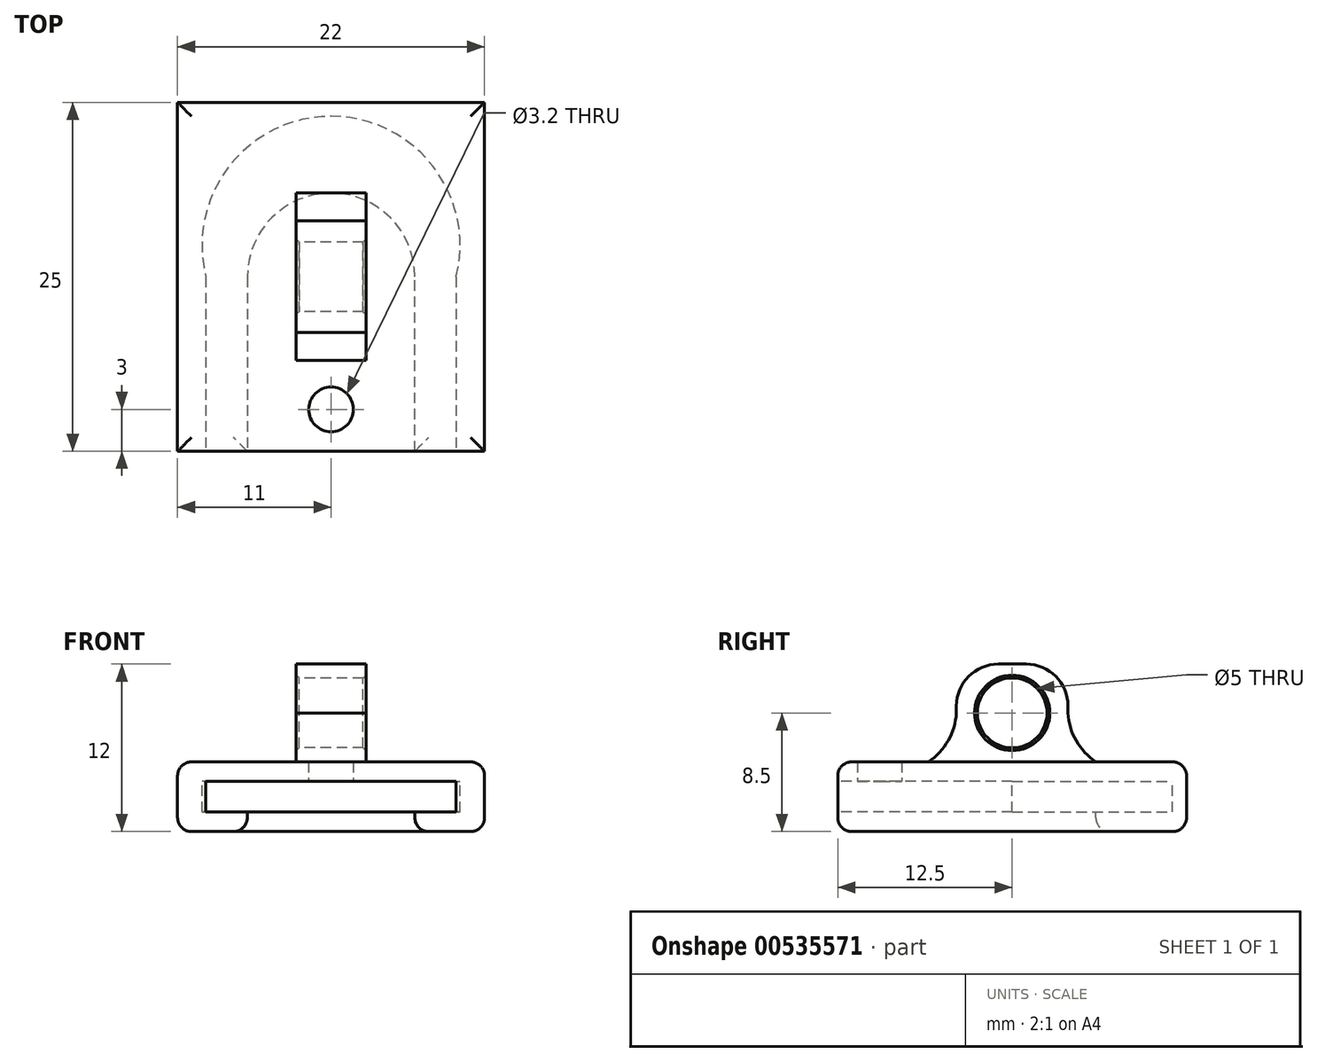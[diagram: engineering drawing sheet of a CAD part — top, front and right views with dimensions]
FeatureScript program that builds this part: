
annotation { "Feature Type Name" : "Feature", "Feature Type Description" : "" }
export const myFeature = defineFeature(function(context is Context, id is Id, definition is map)
    precondition{}
    {
        {
            var Q0;
            Q0=qCreatedBy(makeId("Top.planeOp"),FACE);
            var sketch = newSketch(context, id + "F0", { "sketchPlane" : qUnion([Q0])});
            skLineSegment(sketch, "E0.bottom", {"start": v(-11, 12.5) * mm, "end": v(11, 12.5) * mm});
            skLineSegment(sketch, "E0.top", {"start": v(-11, -12.5) * mm, "end": v(11, -12.5) * mm});
            skLineSegment(sketch, "E0.left", {"start": v(-11, 12.5) * mm, "end": v(-11, -12.5) * mm});
            skLineSegment(sketch, "E0.right", {"start": v(11, 12.5) * mm, "end": v(11, -12.5) * mm});
            skPoint(sketch, "E0.middle", {"position": v(0, 0) * mm});
            skSolve(sketch);
        }
        {
            var Q0;
            Q0 = qSketchRegion(id + "F0", true);
            extrude(context, id + "F1", {"entities" : qUnion([Q0]), "depth" : 5 * mm, "offsetDistance" : 25 * mm, "symmetric" : true});
        }
        {
            var Q0;
            Q0=qCreatedBy(makeId("Top.planeOp"),FACE);
            var sketch = newSketch(context, id + "F2", { "sketchPlane" : qUnion([Q0])});
            skCircle(sketch, "E1", {"center": v(0, 2.25) * mm, "radius": 9.25 * mm});
            skLineSegment(sketch, "E2", {"start": v(-8.97, 0) * mm, "end": v(-8.97, -12.5) * mm});
            skLineSegment(sketch, "E3", {"start": v(8.97, 0) * mm, "end": v(8.97, -12.5) * mm});
            skLineSegment(sketch, "E4", {"start": v(-8.97, -12.5) * mm, "end": v(8.97, -12.5) * mm});
            skSolve(sketch);
        }
        {
            var Q0;
            Q0 = qSketchRegion(id + "F2", true);
            extrude(context, id + "F3", {"entities" : qUnion([Q0]), "operationType" : NewBodyOperationType.REMOVE, "oppositeDirection" : true, "depth" : 2.2 * mm, "offsetDistance" : 25 * mm, "symmetric" : true});
        }
        {
            var Q0;
            Q0=qCreatedBy(makeId("Top.planeOp"),FACE);
            var sketch = newSketch(context, id + "F4", { "sketchPlane" : qUnion([Q0])});
            skCircle(sketch, "E5", {"center": v(0, 0) * mm, "radius": 6 * mm});
            skLineSegment(sketch, "E6", {"start": v(-6, 0) * mm, "end": v(-6, -12.5) * mm});
            skLineSegment(sketch, "E7", {"start": v(-6, -12.5) * mm, "end": v(6, -12.5) * mm});
            skLineSegment(sketch, "E8", {"start": v(6, -12.5) * mm, "end": v(6, 0) * mm});
            skSolve(sketch);
        }
        {
            var Q0;
            Q0 = qSketchRegion(id + "F4", true);
            extrude(context, id + "F5", {"entities" : qUnion([Q0]), "operationType" : NewBodyOperationType.REMOVE, "oppositeDirection" : true, "depth" : 25 * mm, "offsetDistance" : 25 * mm});
        }
        {
            var Q0;
            Q0=qCreatedBy(makeId("Top.planeOp"),FACE);
            var sketch = newSketch(context, id + "F6", { "sketchPlane" : qUnion([Q0])});
            skCircle(sketch, "E9", {"center": v(0, -9.5) * mm, "radius": 1.6 * mm});
            skSolve(sketch);
        }
        {
            var Q0;
            Q0 = qSketchRegion(id + "F6", true);
            extrude(context, id + "F7", {"entities" : qUnion([Q0]), "operationType" : NewBodyOperationType.REMOVE, "depth" : 29.4 * mm, "offsetDistance" : 25 * mm});
        }
        {
            var Q0;
            Q0=qCreatedBy(makeId("Right.planeOp"),FACE);
            var sketch = newSketch(context, id + "F8", { "sketchPlane" : qUnion([Q0])});
            skLineSegment(sketch, "E10.bottom", {"start": v(-1, 9.5) * mm, "end": v(1, 9.5) * mm});
            skLineSegment(sketch, "E10.top", {"start": v(-4, 2.5) * mm, "end": v(4, 2.5) * mm});
            skLineSegment(sketch, "E10.left", {"start": v(-4, 6.5) * mm, "end": v(-4, 2.5) * mm});
            skLineSegment(sketch, "E10.right", {"start": v(4, 6.5) * mm, "end": v(4, 2.5) * mm});
            skCircle(sketch, "E11", {"center": v(0, 6) * mm, "radius": 2.5 * mm});
            skPoint(sketch, "E12.visualSharp", {"position": v(-4, 9.5) * mm});
            skArc(sketch, "E12.filletArc", {"start": v(-1, 9.5) * mm, "mid": v(-3.12, 8.62) * mm, "end": v(-4, 6.5) * mm});
            skPoint(sketch, "E13.visualSharp", {"position": v(4, 9.5) * mm});
            skArc(sketch, "E13.filletArc", {"start": v(4, 6.5) * mm, "mid": v(3.12, 8.62) * mm, "end": v(1, 9.5) * mm});
            skSolve(sketch);
        }
        {
            var Q0;
            Q0 = qSketchRegion(id + "F8", true);
            extrude(context, id + "F9", {"entities" : qUnion([Q0]), "operationType" : NewBodyOperationType.ADD, "depth" : 5 * mm, "offsetDistance" : 25 * mm, "symmetric" : true});
        }
        {
            var Q0;
            Q0=qCreatedBy(makeId("Right.planeOp"),FACE);
            var sketch = newSketch(context, id + "F10", { "sketchPlane" : qUnion([Q0])});
            skLineSegment(sketch, "E14", {"start": v(6, 2.5) * mm, "end": v(4, 2.5) * mm});
            skLineSegment(sketch, "E15", {"start": v(4, 2.5) * mm, "end": v(4, 6.5) * mm});
            skArc(sketch, "E16", {"start": v(4, 6.5) * mm, "mid": v(4.47, 4.23) * mm, "end": v(6, 2.5) * mm});
            skLineSegment(sketch, "E17.MirrorCS", {"start": v(-6, 2.5) * mm, "end": v(-4, 2.5) * mm});
            skLineSegment(sketch, "E18.MirrorCS", {"start": v(-4, 2.5) * mm, "end": v(-4, 6.5) * mm});
            skArc(sketch, "E19.MirrorCS", {"start": v(-4, 6.5) * mm, "mid": v(-4.47, 4.23) * mm, "end": v(-6, 2.5) * mm});
            skSolve(sketch);
        }
        {
            var Q0;
            Q0 = qSketchRegion(id + "F10", true);
            extrude(context, id + "F11", {"entities" : qUnion([Q0]), "operationType" : NewBodyOperationType.ADD, "depth" : 5 * mm, "offsetDistance" : 25 * mm, "symmetric" : true});
        }
        {
            var Q0;
            Q0=makeQuery(id+"F1.opExtrude","CAP_EDGE",EDGE,{"disambiguationData":[OSD([sQuery(id+"F0.wireOp",EDGE,"E0.left")])],"isStart":true});
            var Q1;
            Q1=makeQuery(id+"F1.opExtrude","CAP_EDGE",EDGE,{"disambiguationData":[OSD([sQuery(id+"F0.wireOp",EDGE,"E0.left")])],"isStart":false});
            var Q2;
            Q2=makeQuery(id+"F1.opExtrude","CAP_EDGE",EDGE,{"disambiguationData":[OSD([sQuery(id+"F0.wireOp",EDGE,"E0.right")])],"isStart":false});
            var Q3;
            Q3=makeQuery(id+"F1.opExtrude","CAP_EDGE",EDGE,{"disambiguationData":[OSD([sQuery(id+"F0.wireOp",EDGE,"E0.right")])],"isStart":true});
            var Q4;
            Q4=makeQuery(id+"F1.opExtrude","CAP_EDGE",EDGE,{"disambiguationData":[OSD([sQuery(id+"F0.wireOp",EDGE,"E0.top")])],"isStart":false});
            var Q5;
            Q5=makeQuery(id+"F1.opExtrude","CAP_EDGE",EDGE,{"disambiguationData":[OSD([sQuery(id+"F0.wireOp",EDGE,"E0.bottom")])],"isStart":false});
            var Q6;
            Q6=makeQuery(id+"F1.opExtrude","CAP_EDGE",EDGE,{"disambiguationData":[OSD([sQuery(id+"F0.wireOp",EDGE,"E0.bottom")])],"isStart":true});
            var Q7;
            {var subQ0=sQuery(id+"F0.wireOp",EDGE,"E0.right");var subQ1=sQuery(id+"F0.wireOp",EDGE,"E0.top");Q7=makeQuery(id+"F5.boolean.opBoolean","SPLIT",EDGE,{"disambiguationData":[TD([makeQuery(id+"F1.opExtrude","SWEPT_FACE",FACE,{"disambiguationData":[OSD([subQ0])]})])],"derivedFrom":makeQuery(id+"F1.opExtrude","CAP_EDGE",EDGE,{"disambiguationData":[OSD([subQ1])],"isStart":true})});}
            var Q8;
            {var subQ0=sQuery(id+"F0.wireOp",EDGE,"E0.left");var subQ1=sQuery(id+"F0.wireOp",EDGE,"E0.top");Q8=makeQuery(id+"F5.boolean.opBoolean","SPLIT",EDGE,{"disambiguationData":[TD([makeQuery(id+"F1.opExtrude","SWEPT_FACE",FACE,{"disambiguationData":[OSD([subQ0])]})])],"derivedFrom":makeQuery(id+"F1.opExtrude","CAP_EDGE",EDGE,{"disambiguationData":[OSD([subQ1])],"isStart":true})});}
            var Q9;
            Q9=makeQuery(id+"F5.boolean.opBoolean","INTERSECT",EDGE,{"derivedFrom":[makeQuery(id+"F1.opExtrude","CAP_FACE",FACE,{"disambiguationData":[OSD([sQuery(id+"F0.wireOp",EDGE,"E0.bottom"),sQuery(id+"F0.wireOp",EDGE,"E0.top"),sQuery(id+"F0.wireOp",EDGE,"E0.left"),sQuery(id+"F0.wireOp",EDGE,"E0.right")])],"isStart":true}),makeQuery(id+"F5.opExtrude","SWEPT_FACE",FACE,{"disambiguationData":[OSD([sQuery(id+"F4.wireOp",EDGE,"E8")])]})]});
            fillet(context, id + "F12", {"entities" : qUnion([Q0, Q1, Q2, Q3, Q4, Q5, Q6, Q7, Q8, Q9]), "radius" : 1 * mm, "tangentPropagation" : true, "allowEdgeOverflow" : false});
        }
        {
            var Q0;
            Q0=makeQuery(id+"F9.opExtrude","CAP_EDGE",EDGE,{"disambiguationData":[OSD([sQuery(id+"F8.wireOp",EDGE,"E11")])],"isStart":false});
            var Q1;
            Q1=makeQuery(id+"F9.opExtrude","CAP_EDGE",EDGE,{"disambiguationData":[OSD([sQuery(id+"F8.wireOp",EDGE,"E11")])],"isStart":true});
            chamfer(context, id + "F13", {"entities" : qUnion([Q0, Q1]), "width" : 0.2 * mm, "tangentPropagation" : true});
        }
    });
